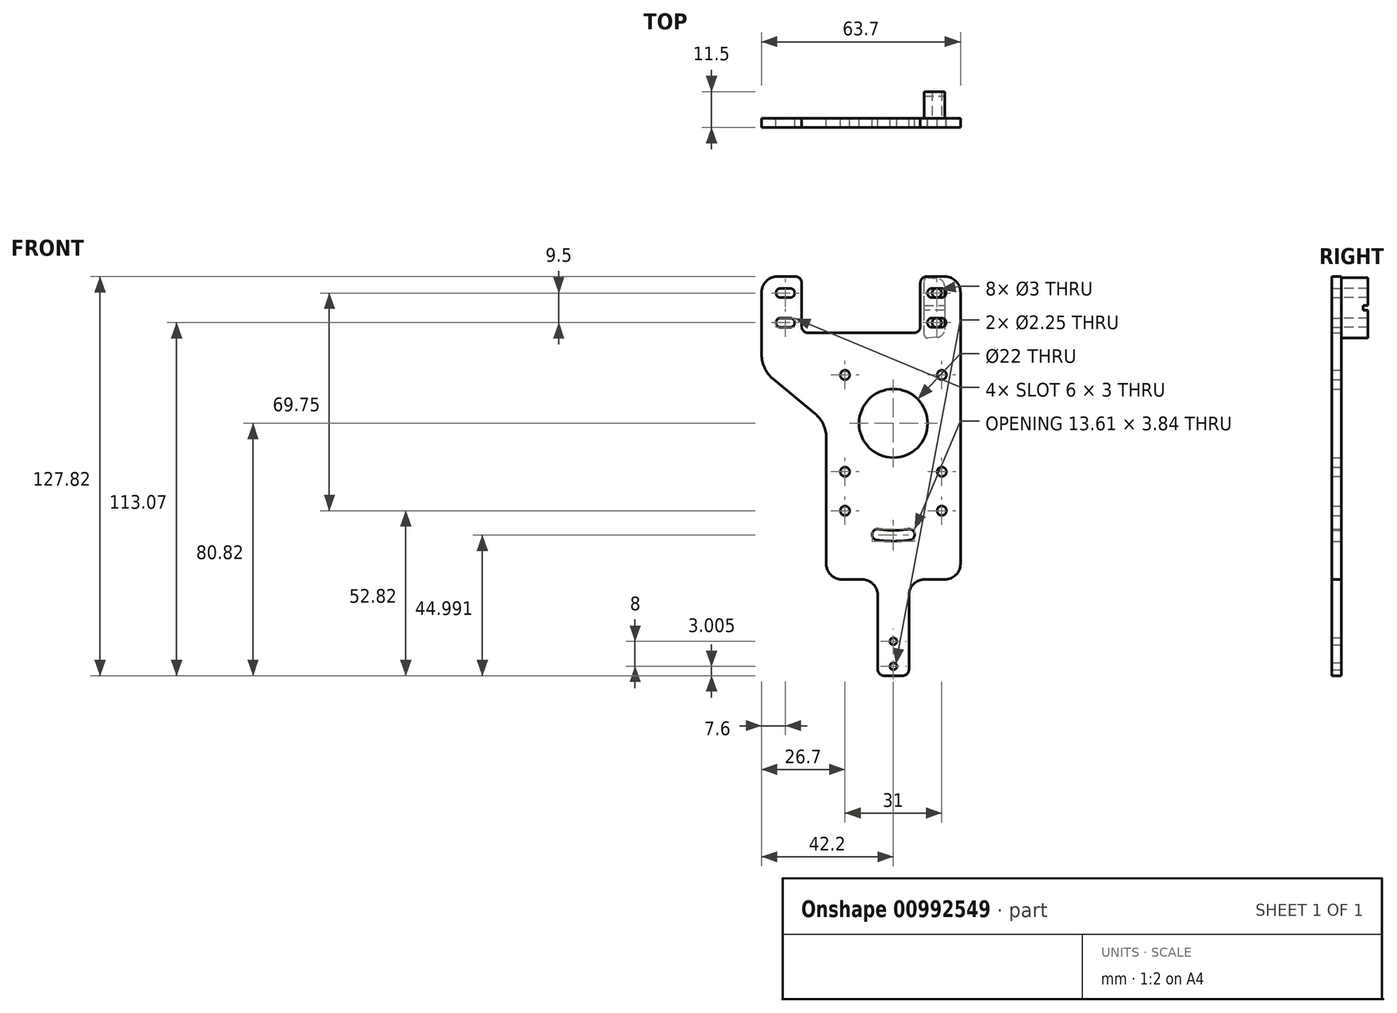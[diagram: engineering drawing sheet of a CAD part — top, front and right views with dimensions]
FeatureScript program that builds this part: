
annotation { "Feature Type Name" : "Feature", "Feature Type Description" : "" }
export const myFeature = defineFeature(function(context is Context, id is Id, definition is map)
    precondition{}
    {
        {
            var Q0;
            Q0=qCreatedBy(makeId("Front.planeOp"),FACE);
            var sketch = newSketch(context, id + "F0", { "sketchPlane" : qUnion([Q0])});
            skLineSegment(sketch, "E0", {"start": v(0, 45.16) * mm, "end": v(0, -78.26) * mm, "construction": true});
            skLineSegment(sketch, "E1", {"start": v(-43, 0) * mm, "end": v(26.64, 0) * mm, "construction": true});
            skCircle(sketch, "E2", {"center": v(0, 0) * mm, "radius": 3.5 * mm, "construction": true});
            skLineSegment(sketch, "E3", {"start": v(-3.05, 24.93) * mm, "end": v(28.89, -79.52) * mm, "construction": true});
            skLineSegment(sketch, "E4", {"start": v(1.45, 7.22) * mm, "end": v(8.27, -15.1) * mm, "construction": true});
            skLineSegment(sketch, "E5", {"start": v(3.28, 7.22) * mm, "end": v(10.1, -15.1) * mm, "construction": true});
            skSolve(sketch);
        }
        {
            var Q0;
            Q0=qCreatedBy(makeId("Front.planeOp"),FACE);
            var sketch = newSketch(context, id + "F1", { "sketchPlane" : qUnion([Q0])});
            skCircle(sketch, "E6", {"center": v(15.5, 15.5) * mm, "radius": 1.5 * mm});
            skLineSegment(sketch, "E7", {"start": v(21.5, -45) * mm, "end": v(21.5, 42) * mm});
            skPoint(sketch, "E8", {"position": v(0, -50) * mm});
            skArc(sketch, "E9", {"start": v(4.83, -33.9) * mm, "mid": v(2.42, -34.16) * mm, "end": v(0, -34.25) * mm});
            skArc(sketch, "E10", {"start": v(5.32, -37.37) * mm, "mid": v(2.67, -37.66) * mm, "end": v(0, -37.75) * mm});
            skArc(sketch, "E11", {"start": v(4.83, -33.9) * mm, "mid": v(6.8, -35.4) * mm, "end": v(5.32, -37.37) * mm});
            skArc(sketch, "E12", {"start": v(8.38, -35) * mm, "mid": v(-0.1, -36) * mm, "end": v(-8.59, -34.96) * mm, "construction": true});
            skCircle(sketch, "E13.MirrorC", {"center": v(15.5, -15.5) * mm, "radius": 1.5 * mm});
            skCircle(sketch, "E14.MirrorC", {"center": v(-15.5, 15.5) * mm, "radius": 1.5 * mm});
            skCircle(sketch, "E15.MirrorC", {"center": v(-15.5, -15.5) * mm, "radius": 1.5 * mm});
            skLineSegment(sketch, "E16.MirrorCS", {"start": v(-21.5, -45) * mm, "end": v(-21.5, -4.56) * mm});
            skArc(sketch, "E17.MirrorCS", {"start": v(-5.32, -37.37) * mm, "mid": v(-2.67, -37.66) * mm, "end": v(0, -37.75) * mm});
            skArc(sketch, "E18.MirrorCS", {"start": v(-4.83, -33.9) * mm, "mid": v(-6.8, -35.4) * mm, "end": v(-5.32, -37.37) * mm});
            skArc(sketch, "E19.MirrorCS", {"start": v(-4.83, -33.9) * mm, "mid": v(-2.42, -34.16) * mm, "end": v(0, -34.25) * mm});
            skLineSegment(sketch, "E20", {"start": v(16.5, 47) * mm, "end": v(10.65, 47) * mm});
            skLineSegment(sketch, "E21", {"start": v(-42.2, 42) * mm, "end": v(-42.2, 22.02) * mm});
            skLineSegment(sketch, "E22", {"start": v(-10.35, 28.4) * mm, "end": v(-10.35, 46.94) * mm, "construction": true});
            skLineSegment(sketch, "E23", {"start": v(22.97, 37) * mm, "end": v(-42.76, 37) * mm, "construction": true});
            skCircle(sketch, "E24", {"center": v(0, 0) * mm, "radius": 11 * mm});
            skLineSegment(sketch, "E25", {"start": v(-16.5, -50) * mm, "end": v(-10, -50) * mm});
            skPoint(sketch, "E26.visualSharp", {"position": v(21.06, 47) * mm});
            skArc(sketch, "E26.filletArc", {"start": v(21.5, 42) * mm, "mid": v(20.04, 45.54) * mm, "end": v(16.5, 47) * mm});
            skPoint(sketch, "E27.visualSharp", {"position": v(-42.2, 47) * mm});
            skArc(sketch, "E27.filletArc", {"start": v(-37.2, 47) * mm, "mid": v(-40.74, 45.54) * mm, "end": v(-42.2, 42) * mm});
            skArc(sketch, "E28", {"start": v(-36.1, 33.75) * mm, "mid": v(-37.6, 32.25) * mm, "end": v(-36.1, 30.75) * mm});
            skLineSegment(sketch, "E29", {"start": v(-38.59, 14.32) * mm, "end": v(-25.11, 3.14) * mm});
            skPoint(sketch, "E30.visualSharp", {"position": v(-21.5, 0.14) * mm});
            skArc(sketch, "E30.filletArc", {"start": v(-21.5, -4.56) * mm, "mid": v(-22.45, -0.3) * mm, "end": v(-25.11, 3.14) * mm});
            skPoint(sketch, "E31.visualSharp", {"position": v(-42.2, 17.32) * mm});
            skArc(sketch, "E31.filletArc", {"start": v(-42.2, 22.02) * mm, "mid": v(-41.25, 17.76) * mm, "end": v(-38.59, 14.32) * mm});
            skArc(sketch, "E32", {"start": v(-33.1, 30.75) * mm, "mid": v(-31.6, 32.25) * mm, "end": v(-33.1, 33.75) * mm});
            skLineSegment(sketch, "E33", {"start": v(-33.1, 33.75) * mm, "end": v(-36.1, 33.75) * mm});
            skLineSegment(sketch, "E34", {"start": v(-33.1, 30.75) * mm, "end": v(-36.1, 30.75) * mm});
            skArc(sketch, "E35.MirrorCS", {"start": v(-36.1, 40.25) * mm, "mid": v(-37.6, 41.75) * mm, "end": v(-36.1, 43.25) * mm});
            skLineSegment(sketch, "E36.MirrorCS", {"start": v(-33.1, 40.25) * mm, "end": v(-36.1, 40.25) * mm});
            skArc(sketch, "E37.MirrorCS", {"start": v(-33.1, 43.25) * mm, "mid": v(-31.6, 41.75) * mm, "end": v(-33.1, 40.25) * mm});
            skLineSegment(sketch, "E38.MirrorCS", {"start": v(-33.1, 43.25) * mm, "end": v(-36.1, 43.25) * mm});
            skArc(sketch, "E39.MirrorCS", {"start": v(12.4, 30.75) * mm, "mid": v(10.9, 32.25) * mm, "end": v(12.4, 33.75) * mm});
            skLineSegment(sketch, "E40.MirrorCS", {"start": v(12.4, 30.75) * mm, "end": v(15.4, 30.75) * mm});
            skLineSegment(sketch, "E41.MirrorCS", {"start": v(12.4, 33.75) * mm, "end": v(15.4, 33.75) * mm});
            skArc(sketch, "E42.MirrorCS", {"start": v(15.4, 33.75) * mm, "mid": v(16.9, 32.25) * mm, "end": v(15.4, 30.75) * mm});
            skLineSegment(sketch, "E43.MirrorCS", {"start": v(12.4, 40.25) * mm, "end": v(15.4, 40.25) * mm});
            skArc(sketch, "E44.MirrorCS", {"start": v(15.4, 40.25) * mm, "mid": v(16.9, 41.75) * mm, "end": v(15.4, 43.25) * mm});
            skArc(sketch, "E45.MirrorCS", {"start": v(12.4, 43.25) * mm, "mid": v(10.9, 41.75) * mm, "end": v(12.4, 40.25) * mm});
            skLineSegment(sketch, "E46.MirrorCS", {"start": v(12.4, 43.25) * mm, "end": v(15.4, 43.25) * mm});
            skCircle(sketch, "E47", {"center": v(5.32, -35.6) * mm, "radius": 1.5 * mm, "construction": true});
            skLineSegment(sketch, "E48", {"start": v(0, 0) * mm, "end": v(6.18, -41.34) * mm, "construction": true});
            skCircle(sketch, "E49", {"center": v(-34.6, 32.25) * mm, "radius": 1.5 * mm, "construction": true});
            skCircle(sketch, "E50.MirrorC", {"center": v(-34.6, 41.75) * mm, "radius": 1.5 * mm, "construction": true});
            skCircle(sketch, "E51.MirrorC", {"center": v(13.9, 32.25) * mm, "radius": 1.5 * mm, "construction": true});
            skCircle(sketch, "E52.MirrorC", {"center": v(13.9, 41.75) * mm, "radius": 1.5 * mm, "construction": true});
            skCircle(sketch, "E53", {"center": v(15.5, -28) * mm, "radius": 1.5 * mm});
            skCircle(sketch, "E54.MirrorC", {"center": v(-15.5, -28) * mm, "radius": 1.5 * mm});
            skLineSegment(sketch, "E55", {"start": v(-27.35, 29) * mm, "end": v(6.65, 29) * mm});
            skLineSegment(sketch, "E56", {"start": v(-29.35, 45) * mm, "end": v(-29.35, 31) * mm});
            skLineSegment(sketch, "E57", {"start": v(8.65, 45) * mm, "end": v(8.65, 31) * mm});
            skLineSegment(sketch, "E58.trimOffspring", {"start": v(-31.35, 47) * mm, "end": v(-37.2, 47) * mm});
            skPoint(sketch, "E59.visualSharp", {"position": v(-29.35, 47) * mm});
            skArc(sketch, "E59.filletArc", {"start": v(-29.35, 45) * mm, "mid": v(-29.94, 46.41) * mm, "end": v(-31.35, 47) * mm});
            skPoint(sketch, "E60.visualSharp", {"position": v(8.65, 47) * mm});
            skArc(sketch, "E60.filletArc", {"start": v(10.65, 47) * mm, "mid": v(9.24, 46.41) * mm, "end": v(8.65, 45) * mm});
            skPoint(sketch, "E61.visualSharp", {"position": v(-29.35, 29) * mm});
            skArc(sketch, "E61.filletArc", {"start": v(-29.35, 31) * mm, "mid": v(-28.76, 29.59) * mm, "end": v(-27.35, 29) * mm});
            skPoint(sketch, "E62.visualSharp", {"position": v(8.65, 29) * mm});
            skArc(sketch, "E62.filletArc", {"start": v(6.65, 29) * mm, "mid": v(8.06, 29.59) * mm, "end": v(8.65, 31) * mm});
            skLineSegment(sketch, "E63", {"start": v(-36.07, -22) * mm, "end": v(-55, -22) * mm, "construction": true});
            skLineSegment(sketch, "E64", {"start": v(-15, -66.45) * mm, "end": v(-53.61, -66.45) * mm, "construction": true});
            skCircle(sketch, "E65", {"center": v(0, -69.82) * mm, "radius": 1.13 * mm});
            skCircle(sketch, "E66", {"center": v(0, -77.82) * mm, "radius": 1.13 * mm});
            skLineSegment(sketch, "E67", {"start": v(-5, -55) * mm, "end": v(-5, -78.82) * mm});
            skLineSegment(sketch, "E68", {"start": v(-3, -80.82) * mm, "end": v(3, -80.82) * mm});
            skLineSegment(sketch, "E69", {"start": v(5, -78.82) * mm, "end": v(5, -55) * mm});
            skLineSegment(sketch, "E70", {"start": v(10, -50) * mm, "end": v(16.5, -50) * mm});
            skPoint(sketch, "E71.visualSharp", {"position": v(-5, -80.82) * mm});
            skArc(sketch, "E71.filletArc", {"start": v(-5, -78.82) * mm, "mid": v(-4.41, -80.23) * mm, "end": v(-3, -80.82) * mm});
            skPoint(sketch, "E72.visualSharp", {"position": v(5, -80.82) * mm});
            skArc(sketch, "E72.filletArc", {"start": v(3, -80.82) * mm, "mid": v(4.41, -80.23) * mm, "end": v(5, -78.82) * mm});
            skPoint(sketch, "E73.visualSharp", {"position": v(-21.5, -50) * mm});
            skArc(sketch, "E73.filletArc", {"start": v(-21.5, -45) * mm, "mid": v(-20.04, -48.54) * mm, "end": v(-16.5, -50) * mm});
            skPoint(sketch, "E74.visualSharp", {"position": v(-5, -50) * mm});
            skArc(sketch, "E74.filletArc", {"start": v(-5, -55) * mm, "mid": v(-6.46, -51.46) * mm, "end": v(-10, -50) * mm});
            skPoint(sketch, "E75.visualSharp", {"position": v(5, -50) * mm});
            skArc(sketch, "E75.filletArc", {"start": v(10, -50) * mm, "mid": v(6.46, -51.46) * mm, "end": v(5, -55) * mm});
            skPoint(sketch, "E76.visualSharp", {"position": v(21.5, -50) * mm});
            skArc(sketch, "E76.filletArc", {"start": v(16.5, -50) * mm, "mid": v(20.04, -48.54) * mm, "end": v(21.5, -45) * mm});
            skSolve(sketch);
        }
        {
            var Q0;
            Q0=qSketchRegion(id+"F1",true);
            extrude(context, id + "F2", {"entities" : qUnion([Q0]), "depth" : 3 * mm});
        }
        {
            var Q0;
            Q0=qCreatedBy(makeId("Front.planeOp"),FACE);
            var sketch = newSketch(context, id + "F3", { "sketchPlane" : qUnion([Q0])});
            skLineSegment(sketch, "E77", {"start": v(16.4, 46.25) * mm, "end": v(16.4, 27.75) * mm});
            skLineSegment(sketch, "E78", {"start": v(16.4, 27.75) * mm, "end": v(9.9, 27.25) * mm});
            skLineSegment(sketch, "E79", {"start": v(9.9, 27.25) * mm, "end": v(9.9, 46.75) * mm});
            skLineSegment(sketch, "E80", {"start": v(9.9, 46.75) * mm, "end": v(16.4, 46.25) * mm});
            skCircle(sketch, "E81", {"center": v(13.9, 32.25) * mm, "radius": 1.5 * mm});
            skCircle(sketch, "E82.MirrorC", {"center": v(13.9, 41.75) * mm, "radius": 1.5 * mm});
            skLineSegment(sketch, "E83", {"start": v(13.9, 47.55) * mm, "end": v(13.9, 25.9) * mm, "construction": true});
            skSolve(sketch);
        }
        {
            var Q0;
            Q0=qSketchRegion(id+"F3",true);
            extrude(context, id + "F4", {"entities" : qUnion([Q0]), "oppositeDirection" : true, "depth" : 8.5 * mm, "offsetDistance" : 25 * mm});
        }
        {
            var Q0;
            Q0=makeQuery(id+"F4.opExtrude","CAP_FACE",FACE,{"disambiguationData":[OSD([sQuery(id+"F3.wireOp",EDGE,"E77"),sQuery(id+"F3.wireOp",EDGE,"E78"),sQuery(id+"F3.wireOp",EDGE,"E79"),sQuery(id+"F3.wireOp",EDGE,"E80"),sQuery(id+"F3.wireOp",EDGE,"E81"),sQuery(id+"F3.wireOp",EDGE,"E82.MirrorC")])],"isStart":false});
            var sketch = newSketch(context, id + "F5", { "sketchPlane" : qUnion([Q0])});
            skLineSegment(sketch, "E84", {"start": v(40.1, -4.41) * mm, "end": v(22.9, -4.41) * mm, "construction": true});
            skLineSegment(sketch, "E85", {"start": v(-9.9, 36.25) * mm, "end": v(-9.9, 37.75) * mm});
            skLineSegment(sketch, "E86", {"start": v(-9.9, 37.75) * mm, "end": v(-16.4, 37.75) * mm});
            skLineSegment(sketch, "E87", {"start": v(-16.4, 37.75) * mm, "end": v(-16.4, 36.25) * mm});
            skLineSegment(sketch, "E88", {"start": v(-16.4, 36.25) * mm, "end": v(-9.9, 36.25) * mm});
            skSolve(sketch);
        }
        {
            var Q0;
            Q0=qSketchRegion(id+"F5",true);
            extrude(context, id + "F6", {"entities" : qUnion([Q0]), "operationType" : NewBodyOperationType.REMOVE, "oppositeDirection" : true, "depth" : 1.5 * mm});
        }
        {
            var Q0;
            Q0=makeQuery(id+"F4.opExtrude","SWEPT_EDGE",EDGE,{"disambiguationData":[OSD([sQuery(id+"F3.wireOp",EDGE,"E79"),sQuery(id+"F3.wireOp",EDGE,"E80")])]});
            var Q1;
            Q1=makeQuery(id+"F4.opExtrude","SWEPT_EDGE",EDGE,{"disambiguationData":[OSD([sQuery(id+"F3.wireOp",EDGE,"E78"),sQuery(id+"F3.wireOp",EDGE,"E79")])]});
            fillet(context, id + "F7", {"entities" : qUnion([Q0, Q1]), "radius" : 1 * mm, "tangentPropagation" : true, "allowEdgeOverflow" : false});
        }
        {
            var Q0;
            Q0=makeQuery(id+"F4.opExtrude","SWEPT_EDGE",EDGE,{"disambiguationData":[OSD([sQuery(id+"F3.wireOp",EDGE,"E77"),sQuery(id+"F3.wireOp",EDGE,"E78")])]});
            var Q1;
            Q1=makeQuery(id+"F4.opExtrude","SWEPT_EDGE",EDGE,{"disambiguationData":[OSD([sQuery(id+"F3.wireOp",EDGE,"E77"),sQuery(id+"F3.wireOp",EDGE,"E80")])]});
            fillet(context, id + "F8", {"entities" : qUnion([Q0, Q1]), "radius" : 2.5 * mm, "tangentPropagation" : true, "allowEdgeOverflow" : false});
        }
    });
